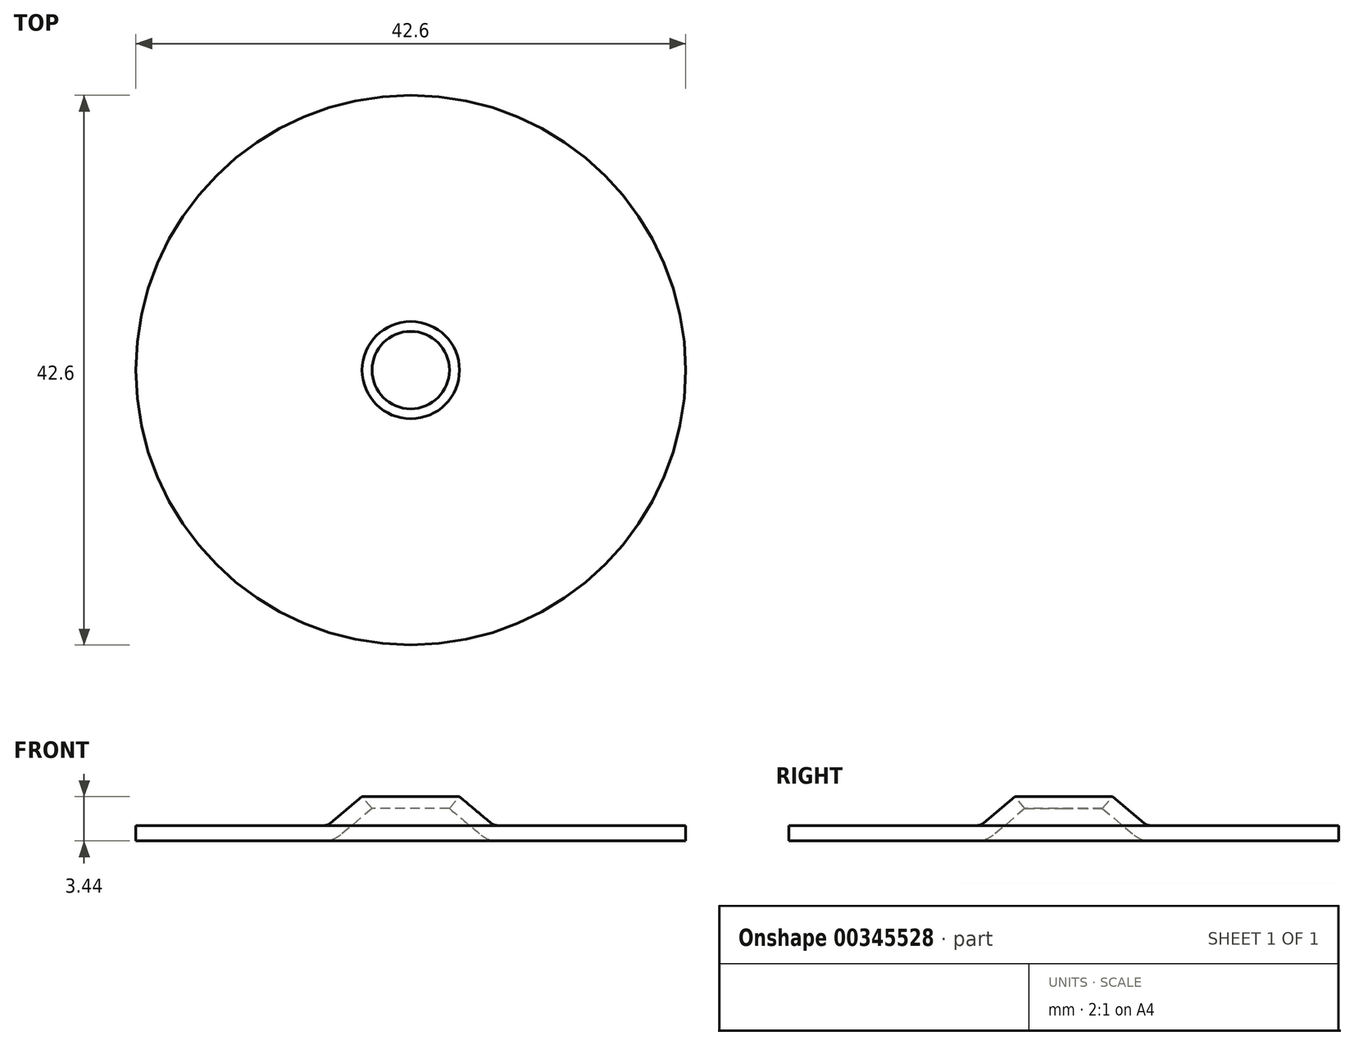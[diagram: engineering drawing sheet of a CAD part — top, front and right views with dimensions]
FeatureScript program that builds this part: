
annotation { "Feature Type Name" : "Feature", "Feature Type Description" : "" }
export const myFeature = defineFeature(function(context is Context, id is Id, definition is map)
    precondition{}
    {
        {
            var Q0;
            Q0=qCreatedBy(makeId("Front.planeOp"),FACE);
            var sketch = newSketch(context, id + "F0", { "sketchPlane" : qUnion([Q0])});
            skLineSegment(sketch, "E0", {"start": v(3, 2.52) * mm, "end": v(5.44, 0.47) * mm});
            skLineSegment(sketch, "E1", {"start": v(6.73, 0) * mm, "end": v(21.3, 0) * mm});
            skPoint(sketch, "E2.visualSharp", {"position": v(6, 0) * mm});
            skArc(sketch, "E2.filletArc", {"start": v(5.44, 0.47) * mm, "mid": v(6.04, 0.12) * mm, "end": v(6.73, 0) * mm});
            skLineSegment(sketch, "E3.0", {"start": v(6.73, 1.2) * mm, "end": v(21.3, 1.2) * mm});
            skArc(sketch, "E3.1", {"start": v(6.21, 1.39) * mm, "mid": v(6.45, 1.25) * mm, "end": v(6.73, 1.2) * mm});
            skLineSegment(sketch, "E3.2", {"start": v(3.77, 3.44) * mm, "end": v(6.21, 1.39) * mm});
            skLineSegment(sketch, "E4", {"start": v(21.3, 0) * mm, "end": v(21.3, 1.2) * mm});
            skLineSegment(sketch, "E5", {"start": v(0, 0) * mm, "end": v(0, -6.93) * mm, "construction": true});
            skLineSegment(sketch, "E6", {"start": v(3.77, 3.44) * mm, "end": v(3, 2.52) * mm});
            skPoint(sketch, "E7.start.orphan", {"position": v(3, 2.52) * mm});
            skSolve(sketch);
        }
        {
            var Q0;
            Q0=makeQuery(id+"F0.imprint","IMPRINT",FACE,{"disambiguationData":[TD([[makeQuery(id+"F0.imprint","IMPRINT",EDGE,{"derivedFrom":sQuery(id+"F0.wireOp",EDGE,"E0")}),1.0]])]});
            var Q1;
            Q1=sQuery(id+"F0.wireOp",EDGE,"E5");
            revolve(context, id + "F1", {"entities" : qUnion([Q0]), "axis" : qUnion([Q1]), "revolveType" : RevolveType.FULL});
        }
    });
